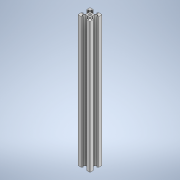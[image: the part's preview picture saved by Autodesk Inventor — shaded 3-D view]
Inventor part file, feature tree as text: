
AUTODESK INVENTOR PART (.ipt)
format: ipt  version: 2021 (Build 250183000, 183)  size: 234,496 bytes
history: native  units: mm
features: sketch x3, extrude x2, fillet x2, other x1, pattern_circular x1, hole x1, projected_geometry x1
ambient origin geometry x8: Origin, YZ Plane, XZ Plane, XY Plane, X Axis, Y Axis, Z Axis, Center Point
bodies: Body1 (feature_tree)
feature tree (11):
  other  "實體1"
  extrude  "擠出1"  Depth=20.0mm
  extrude  "擠出2"  Depth=20.0mm
  fillet  "圓角1"  Radius=216.0mm
  pattern_circular  "環形陣列1"  [2 undecoded]
  hole  "孔1"  [1 undecoded]
  fillet  "圓角2"  Radius=6.2mm
  sketch  "草圖1"
  sketch  "草圖2"
  projected_geometry  "投影迴路1"
  sketch  "草圖3"
note: 3 required parameter values undecoded (feature->parameter linkage not recoverable at this tier; creation-order binding heuristic only, values carry confidence <= 0.55)
